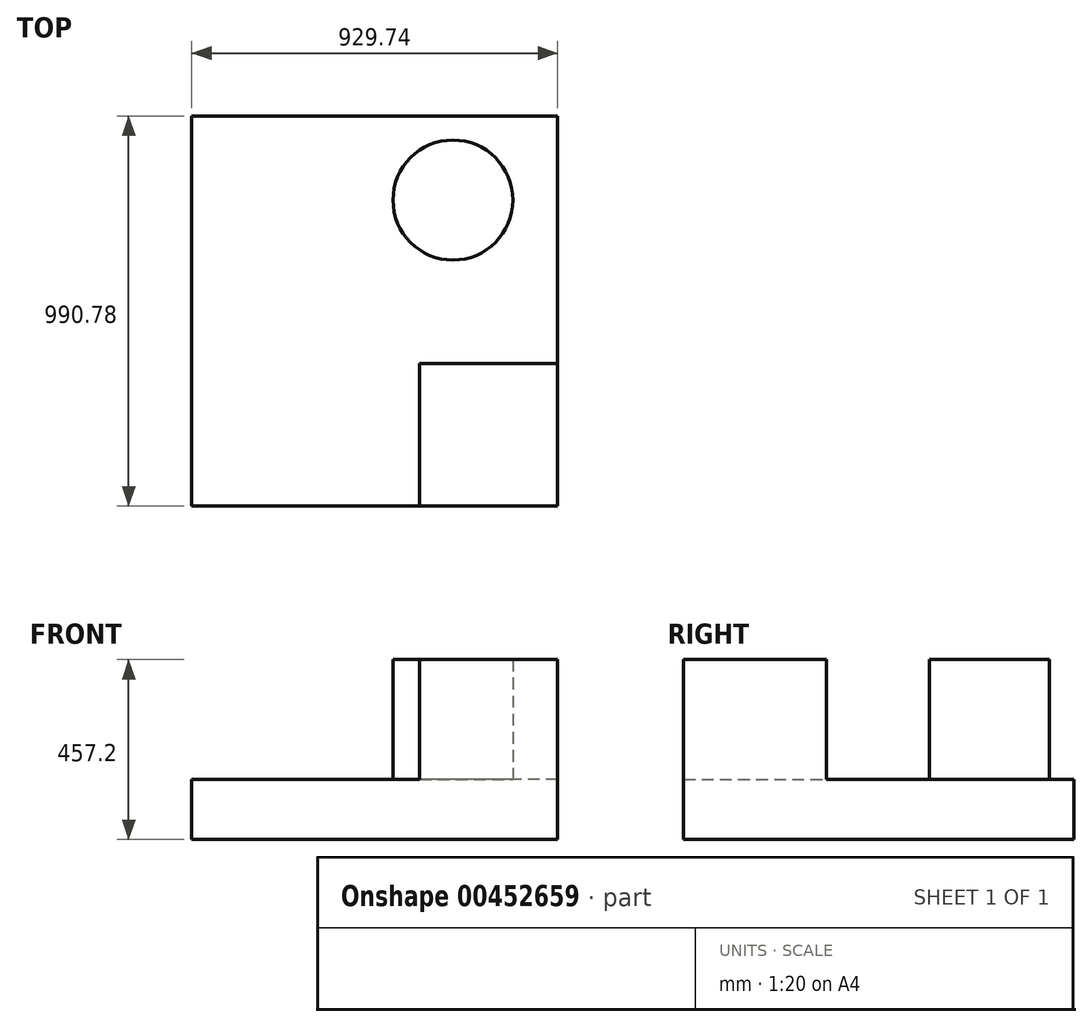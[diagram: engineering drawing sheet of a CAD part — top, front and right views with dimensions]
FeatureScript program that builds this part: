
annotation { "Feature Type Name" : "Feature", "Feature Type Description" : "" }
export const myFeature = defineFeature(function(context is Context, id is Id, definition is map)
    precondition{}
    {
        {
            var Q0;
            Q0=qCreatedBy(makeId("Top.planeOp"),FACE);
            var sketch = newSketch(context, id + "F0", { "sketchPlane" : qUnion([Q0])});
            skLineSegment(sketch, "E0.bottom", {"start": v(-406.7, -249.83) * mm, "end": v(523.04, -249.83) * mm});
            skLineSegment(sketch, "E0.top", {"start": v(-406.7, -1240.6) * mm, "end": v(523.04, -1240.6) * mm});
            skLineSegment(sketch, "E0.left", {"start": v(-406.7, -249.83) * mm, "end": v(-406.7, -1240.6) * mm});
            skLineSegment(sketch, "E0.right", {"start": v(523.04, -249.83) * mm, "end": v(523.04, -1240.6) * mm});
            skSolve(sketch);
        }
        {
            var Q0;
            Q0 = qSketchRegion(id + "F0", true);
            extrude(context, id + "F1", {"entities" : qUnion([Q0]), "depth" : 152.4 * mm});
        }
        {
            var Q0;
            Q0=makeQuery(id+"F1.opExtrude","CAP_FACE",FACE,{"disambiguationData":[OSD([sQuery(id+"F0.wireOp",EDGE,"E0.bottom"),sQuery(id+"F0.wireOp",EDGE,"E0.top"),sQuery(id+"F0.wireOp",EDGE,"E0.left"),sQuery(id+"F0.wireOp",EDGE,"E0.right")])],"isStart":false});
            var sketch = newSketch(context, id + "F2", { "sketchPlane" : qUnion([Q0])});
            skCircle(sketch, "E1", {"center": v(256.94, -463.3) * mm, "radius": 152.4 * mm});
            skSolve(sketch);
        }
        {
            var Q0;
            Q0=makeQuery(id+"F2.imprint","IMPRINT",FACE,{"disambiguationData":[TD([[makeQuery(id+"F2.imprint","IMPRINT",EDGE,{"derivedFrom":sQuery(id+"F2.wireOp",EDGE,"E1")}),1.0]])]});
            extrude(context, id + "F3", {"entities" : qUnion([Q0]), "depth" : 304.8 * mm});
        }
        {
            var Q0;
            Q0=makeQuery(id+"F1.opExtrude","CAP_FACE",FACE,{"disambiguationData":[OSD([sQuery(id+"F0.wireOp",EDGE,"E0.bottom"),sQuery(id+"F0.wireOp",EDGE,"E0.top"),sQuery(id+"F0.wireOp",EDGE,"E0.left"),sQuery(id+"F0.wireOp",EDGE,"E0.right")])],"isStart":false});
            var sketch = newSketch(context, id + "F4", { "sketchPlane" : qUnion([Q0])});
            skLineSegment(sketch, "E2.bottom", {"start": v(523.04, -1240.6) * mm, "end": v(171.98, -1240.6) * mm});
            skLineSegment(sketch, "E2.top", {"start": v(523.04, -878.02) * mm, "end": v(171.98, -878.02) * mm});
            skLineSegment(sketch, "E2.left", {"start": v(523.04, -1240.6) * mm, "end": v(523.04, -878.02) * mm});
            skLineSegment(sketch, "E2.right", {"start": v(171.98, -1240.6) * mm, "end": v(171.98, -878.02) * mm});
            skSolve(sketch);
        }
        {
            var Q0;
            Q0 = qSketchRegion(id + "F4", true);
            extrude(context, id + "F5", {"entities" : qUnion([Q0]), "operationType" : NewBodyOperationType.ADD, "depth" : 304.8 * mm});
        }
    });
